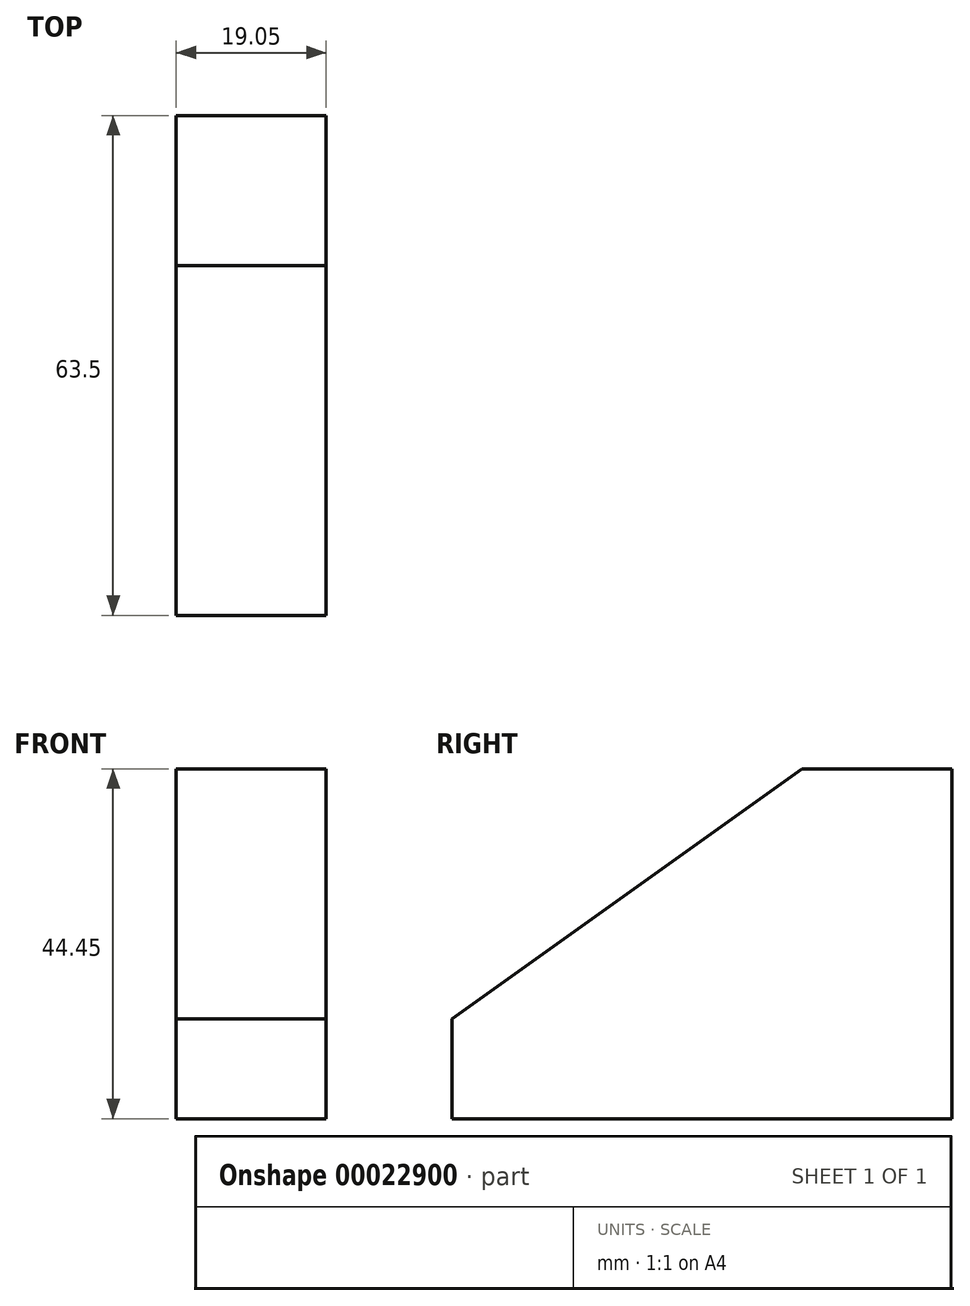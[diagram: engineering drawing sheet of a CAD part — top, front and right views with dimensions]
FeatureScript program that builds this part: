
annotation { "Feature Type Name" : "Feature", "Feature Type Description" : "" }
export const myFeature = defineFeature(function(context is Context, id is Id, definition is map)
    precondition{}
    {
        {
            var Q0;
            Q0=qCreatedBy(makeId("Right.planeOp"),FACE);
            var sketch = newSketch(context, id + "F0", { "sketchPlane" : qUnion([Q0])});
            skLineSegment(sketch, "E0", {"start": v(-15.23, -24.1) * mm, "end": v(48.27, -24.1) * mm});
            skLineSegment(sketch, "E1", {"start": v(48.27, -24.1) * mm, "end": v(48.27, 20.36) * mm});
            skLineSegment(sketch, "E2", {"start": v(48.27, 20.36) * mm, "end": v(29.22, 20.36) * mm});
            skLineSegment(sketch, "E3", {"start": v(-15.23, -24.1) * mm, "end": v(-15.23, -11.4) * mm});
            skLineSegment(sketch, "E4", {"start": v(-15.23, -11.4) * mm, "end": v(29.22, 20.36) * mm});
            skSolve(sketch);
        }
        {
            var Q0;
            Q0 = qSketchRegion(id + "F0", true);
            extrude(context, id + "F1", {"entities" : qUnion([Q0]), "depth" : 19.05 * mm});
        }
    });
